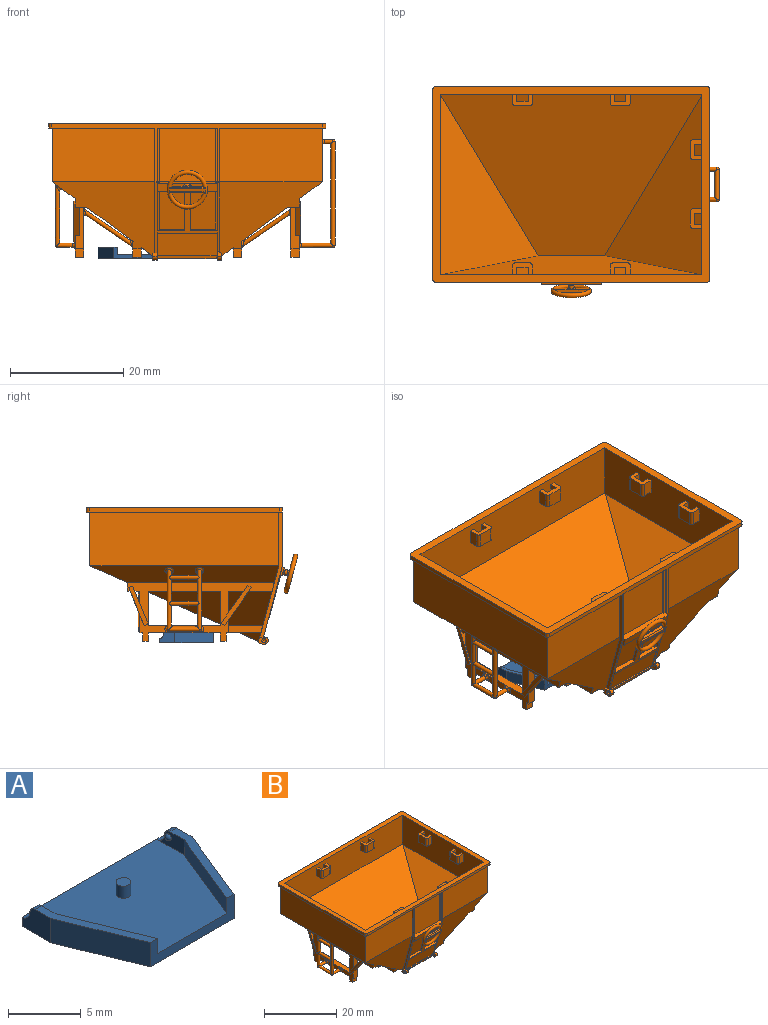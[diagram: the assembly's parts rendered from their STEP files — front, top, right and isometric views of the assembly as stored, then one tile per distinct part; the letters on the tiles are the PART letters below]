
ASSEMBLY  parts=2 mates=2
PART A: 22 faces, bbox 13.7x9.7x2 mm
  f0: plane 12.45x9.65mm, normal (0,0,1), area 99.5mm2, adj f3,f7,f8,f10,f11,f15,f20
  f1: plane 2.79x2.03mm, normal (-1,0,0), area 4.8mm2, adj f2,f6,f9,f15,f16,f19
  f2: plane 6.86x2.79mm, normal (-0.93,-0.38,0), area 15mm2, adj f1,f3,f6,f9
  f3: plane 8.13x2.03mm, normal (0,-1,0), area 7.9mm2, adj f0,f2,f4,f6,f8,f9,f10,f12
  f4: plane 6.86x2.79mm, normal (0.93,-0.38,0), area 15mm2, adj f3,f5,f6,f12
  f5: plane 2.79x2.03mm, normal (1,0,0), area 4.8mm2, adj f4,f6,f12,f15,f17,f18
  f6: plane 13.72x9.65mm, normal (0,0,-1), area 113.2mm2, adj f1,f2,f3,f4,f5,f15
  f7: plane 2.67x1.27mm, normal (1,0,0), area 2.3mm2, adj f0,f8,f9,f14,f16,f19
  f8: plane 6.98x2.84mm, normal (0.93,0.38,0), area 9.6mm2, adj f0,f3,f7,f9
  f9: plane 8.38x3.48mm, normal (0,0,1), area 5.7mm2, adj f1,f2,f3,f7,f8,f19
  f10: plane 6.98x2.84mm, normal (-0.93,0.38,0), area 9.6mm2, adj f0,f3,f11,f12
  f11: plane 2.67x1.27mm, normal (-1,0,0), area 2.3mm2, adj f0,f10,f12,f13,f17,f18
  f12: plane 8.38x3.48mm, normal (0,0,1), area 5.7mm2, adj f3,f4,f5,f10,f11,f18
  f13: sphere r=0.25mm, area 0.4mm2, adj f11
  f14: sphere r=0.25mm, area 0.4mm2, adj f7
  f15: plane 13.72x0.76mm, normal (0,1,0), area 10.5mm2, adj f0,f1,f5,f6,f16,f17
  f16: cylinder r=0.76mm len=0.76mm, axis (-1,0,0), area 0.8mm2, adj f1,f7,f15,f19
  f17: cylinder r=0.76mm len=0.76mm, axis (-1,0,0), area 0.8mm2, adj f5,f11,f15,f18
  f18: cylinder r=0.51mm len=0.64mm, axis (1,0,0), area 0.5mm2, adj f5,f11,f12,f17
  f19: cylinder r=0.51mm len=0.64mm, axis (1,0,0), area 0.5mm2, adj f1,f7,f9,f16
  f20: cylinder r=0.51mm len=1.02mm, axis (0,0,-1), area 3.2mm2, adj f0,f21
  f21: plane 1.02x1.02mm, normal (0,0,1), area 0.8mm2, adj f20
PART B: 349 faces, bbox 50.9x37.7x24.5 mm
  f0: plane 46.1x10.19mm, normal (0,1,0), area 461.8mm2, adj f1,f5,f7,f11,f13,f36,f37,f38
  f1: plane 2.54x1.52mm, normal (1,0,0), area 3.9mm2, adj f0,f2,f346,f348
  f2: cylinder r=0.51mm len=2.54mm, axis (0,0,-1), area 2mm2, adj f1,f3,f346,f348
  f3: plane 2.54x2.54mm, normal (0,1,0), area 6.5mm2, adj f2,f4,f346,f348
  f4: cylinder r=0.51mm len=2.54mm, axis (0,0,-1), area 2mm2, adj f3,f346,f347,f348
  f5: plane 2.54x1.27mm, normal (-1,0,0), area 3.2mm2, adj f0,f6,f346,f348
  f6: plane 2.54x2.03mm, normal (0,-1,0), area 5.2mm2, adj f5,f345,f346,f348
  f7: plane 2.54x1.52mm, normal (1,0,0), area 3.9mm2, adj f0,f8,f342,f344
  f8: cylinder r=0.51mm len=2.54mm, axis (0,0,-1), area 2mm2, adj f7,f9,f342,f344
  f9: plane 2.54x2.54mm, normal (0,1,0), area 6.5mm2, adj f8,f10,f342,f344
  f10: cylinder r=0.51mm len=2.54mm, axis (0,0,-1), area 2mm2, adj f9,f342,f343,f344
  f11: plane 2.54x1.27mm, normal (-1,0,0), area 3.2mm2, adj f0,f12,f342,f344
  f12: plane 2.54x2.03mm, normal (0,-1,0), area 5.2mm2, adj f11,f341,f342,f344
  f13: plane 31.57x17.18mm, normal (0.59,0,0.81), area 337.7mm2, adj f0,f14,f36,f340
  f14: plane 46.1x28.5mm, normal (0,-0.41,0.91), area 907.7mm2, adj f13,f15,f36,f37,f38,f340
  f15: plane 46.1x9.79mm, normal (0,-1,0), area 443.7mm2, adj f14,f16,f20,f22,f23,f24,f25,f26
  f16: plane 2.54x1.52mm, normal (1,0,0), area 3.9mm2, adj f15,f17,f22,f24
  f17: cylinder r=0.51mm len=2.54mm, axis (0,0,-1), area 2mm2, adj f16,f18,f22,f24
  f18: plane 2.54x2.54mm, normal (0,-1,0), area 6.5mm2, adj f17,f19,f22,f24
  f19: cylinder r=0.51mm len=2.54mm, axis (0,0,-1), area 2mm2, adj f18,f22,f24,f25
  f20: plane 2.54x1.27mm, normal (-1,0,0), area 3.2mm2, adj f15,f21,f22,f24
  f21: plane 2.54x2.03mm, normal (0,1,0), area 5.2mm2, adj f20,f22,f23,f24
  f22: plane 3.56x2.03mm, normal (0,0,-1), area 4.5mm2, adj f15,f16,f17,f18,f19,f20,f21,f23
  f23: plane 2.54x1.27mm, normal (1,0,0), area 3.2mm2, adj f15,f21,f22,f24
  f24: plane 3.56x2.03mm, normal (0,0,1), area 4.5mm2, adj f15,f16,f17,f18,f19,f20,f21,f23
  f25: plane 2.54x1.52mm, normal (-1,0,0), area 3.9mm2, adj f15,f19,f22,f24
  f26: plane 2.54x1.52mm, normal (1,0,0), area 3.9mm2, adj f15,f27,f32,f34
  f27: cylinder r=0.51mm len=2.54mm, axis (0,0,-1), area 2mm2, adj f26,f28,f32,f34
  f28: plane 2.54x2.54mm, normal (0,-1,0), area 6.5mm2, adj f27,f29,f32,f34
  f29: cylinder r=0.51mm len=2.54mm, axis (0,0,-1), area 2mm2, adj f28,f32,f34,f35
  f30: plane 2.54x1.27mm, normal (-1,0,0), area 3.2mm2, adj f15,f31,f32,f34
  f31: plane 2.54x2.03mm, normal (0,1,0), area 5.2mm2, adj f30,f32,f33,f34
  f32: plane 3.56x2.03mm, normal (0,0,-1), area 4.5mm2, adj f15,f26,f27,f28,f29,f30,f31,f33
  f33: plane 2.54x1.27mm, normal (1,0,0), area 3.2mm2, adj f15,f31,f32,f34
  f34: plane 3.56x2.03mm, normal (0,0,1), area 4.5mm2, adj f15,f26,f27,f28,f29,f30,f31,f33
  f35: plane 2.54x1.52mm, normal (-1,0,0), area 3.9mm2, adj f15,f29,f32,f34
  f36: plane 45.33x12.37mm, normal (0,0.97,0.26), area 365.5mm2, adj f0,f13,f14,f37
  f37: plane 31.57x17.18mm, normal (-0.59,0,0.81), area 337.7mm2, adj f0,f14,f36,f38
  f38: plane 31.81x9.9mm, normal (-1,0,0), area 307.3mm2, adj f0,f14,f15,f37,f39,f43,f45,f46
  f39: plane 2.54x1.52mm, normal (0,-1,0), area 3.9mm2, adj f38,f40,f45,f47
  f40: cylinder r=0.51mm len=2.54mm, axis (0,0,-1), area 2mm2, adj f39,f41,f45,f47
  f41: plane 2.54x2.54mm, normal (-1,0,0), area 6.5mm2, adj f40,f42,f45,f47
  f42: cylinder r=0.51mm len=2.54mm, axis (0,0,-1), area 2mm2, adj f41,f45,f47,f48
  f43: plane 2.54x1.27mm, normal (0,1,0), area 3.2mm2, adj f38,f44,f45,f47
  f44: plane 2.54x2.03mm, normal (1,0,0), area 5.2mm2, adj f43,f45,f46,f47
  f45: plane 3.56x2.03mm, normal (0,0,-1), area 4.5mm2, adj f38,f39,f40,f41,f42,f43,f44,f46
  f46: plane 2.54x1.27mm, normal (0,-1,0), area 3.2mm2, adj f38,f44,f45,f47
  f47: plane 3.56x2.03mm, normal (0,0,1), area 4.5mm2, adj f38,f39,f40,f41,f42,f43,f44,f46
  f48: plane 2.54x1.52mm, normal (0,1,0), area 3.9mm2, adj f38,f42,f45,f47
  f49: plane 2.54x1.52mm, normal (0,1,0), area 3.9mm2, adj f38,f50,f56,f58
  f50: cylinder r=0.51mm len=2.54mm, axis (0,0,-1), area 2mm2, adj f49,f51,f56,f58
  f51: plane 2.54x2.54mm, normal (-1,0,0), area 6.5mm2, adj f50,f52,f56,f58
  f52: cylinder r=0.51mm len=2.54mm, axis (0,0,-1), area 2mm2, adj f51,f56,f57,f58
  f53: plane 2.54x1.27mm, normal (0,-1,0), area 3.2mm2, adj f38,f54,f56,f58
  f54: plane 2.54x2.03mm, normal (1,0,0), area 5.2mm2, adj f53,f55,f56,f58
  f55: plane 2.54x1.27mm, normal (0,1,0), area 3.2mm2, adj f38,f54,f56,f58
  f56: plane 3.56x2.03mm, normal (0,0,-1), area 4.5mm2, adj f38,f49,f50,f51,f52,f53,f54,f55
  f57: plane 2.54x1.52mm, normal (0,-1,0), area 3.9mm2, adj f38,f52,f56,f58
  f58: plane 3.56x2.03mm, normal (0,0,1), area 4.5mm2, adj f38,f49,f50,f51,f52,f53,f54,f55
  f59: plane 48.9x34.61mm, normal (0,0,1), area 225.3mm2, adj f0,f15,f38,f60,f333,f334,f335,f336
  f60: cylinder r=0.51mm len=0.76mm, axis (0,0,-1), area 0.6mm2, adj f59,f61,f333,f339
  f61: plane 48.9x34.61mm, normal (0,0,-1), area 97mm2, adj f60,f62,f327,f328,f329,f330,f331,f332
  f62: plane 22.1x4mm, normal (-1,0,0), area 14.3mm2, adj f61,f63,f324,f325,f326,f327,f339
  f63: cylinder r=0.64mm len=0.38mm, axis (1,0,0), area 0.1mm2, adj f62,f64,f324,f339
  f64: plane 9.69x0.39mm, normal (1,0,0), area 3.7mm2, adj f63,f65,f321,f322,f323,f339
  f65: plane 10.67x0.64mm, normal (0,0,-1), area 6.6mm2, adj f64,f66,f317,f318,f319,f320,f321,f339
  f66: plane 9.69x0.39mm, normal (-1,0,0), area 3.7mm2, adj f65,f67,f68,f317,f323,f339
  f67: cylinder r=0.25mm len=0.38mm, axis (1,0,0), area 0mm2, adj f66,f317,f318,f323
  f68: cylinder r=0.64mm len=0.38mm, axis (1,0,0), area 0.1mm2, adj f66,f69,f332,f339
  f69: plane 12.09x3.24mm, normal (0,-0.97,-0.26), area 4.8mm2, adj f68,f70,f313,f314,f315,f316,f332
  f70: plane 0.52x0.25mm, normal (1,0,0), area 0.1mm2, adj f69,f71,f261,f312
  f71: plane 10.67x0.25mm, normal (0,0.26,-0.97), area 2.7mm2, adj f70,f72,f259,f260,f261,f316
  f72: plane 4.78x1.17mm, normal (1,0,0), area 1.5mm2, adj f71,f73,f255,f256,f257,f258,f260,f324
  f73: cylinder r=0.76mm len=0.96mm, axis (1,0,0), area 1.1mm2, adj f72,f74,f255,f258
  f74: plane 1.79x1.26mm, normal (-1,0,0), area 1.4mm2, adj f73,f75,f253,f255,f258,f325,f326
  f75: plane 1.02x0.53mm, normal (0,0.97,0.26), area 0.3mm2, adj f74,f76,f77,f252,f258
  f76: cylinder r=0.25mm len=0.8mm, axis (0,0.97,0.26), area 0.3mm2, adj f75,f77,f257,f258
  f77: plane 10.84x0.85mm, normal (0,0.26,-0.97), area 9.1mm2, adj f75,f76,f78,f251,f252,f257
  f78: cylinder r=0.25mm len=1.15mm, axis (0,-0.97,-0.26), area 0.4mm2, adj f77,f79,f247,f248,f249,f251
  f79: plane 0.76x0.15mm, normal (0,0.97,0.26), area 0mm2, adj f78,f80,f246,f247,f251
  f80: plane 1.97x1.26mm, normal (1,0,0), area 1.4mm2, adj f79,f81,f241,f242,f243,f244,f246,f247
  f81: plane 18.13x13.08mm, normal (0,-0.97,-0.26), area 127.6mm2, adj f80,f82,f177,f234,f235,f236,f237,f238
  f82: plane 33.34x4mm, normal (0.59,0,-0.81), area 147.4mm2, adj f81,f83,f177,f330
  f83: plane 47.63x6.58mm, normal (0,0.41,-0.91), area 314.5mm2, adj f82,f84,f176,f329
  f84: plane 33.34x4mm, normal (-0.59,0,-0.81), area 142.8mm2, adj f83,f85,f174,f175,f326,f328
  f85: plane 25.97x10.39mm, normal (-1,0,0), area 67.3mm2, adj f84,f86,f131,f132,f149,f150,f151,f152
  f86: plane 6.07x1.52mm, normal (0,1,0), area 9.2mm2, adj f85,f87,f173,f234
  f87: plane 15.75x8.86mm, normal (1,0,0), area 40.1mm2, adj f86,f88,f131,f149,f150,f151,f152,f155
  f88: bspline ~1.54x1.27mm, area 1.4mm2, adj f87,f89
  f89: cylinder r=0.38mm len=9.28mm, axis (-0.83,0,0.56), area 23.6mm2, adj f88,f90
  f90: bspline ~1.54x1.27mm, area 1.4mm2, adj f89,f91
  f91: plane 22.08x9.22mm, normal (-1,0,0), area 38.2mm2, adj f90,f92,f119,f120,f121,f122,f123,f124
  f92: plane 35.5x19.6mm, normal (0,0.41,-0.91), area 501.5mm2, adj f91,f93,f94,f95,f119,f120,f234,f235
  f93: plane 5.92x1.52mm, normal (0,-1,0), area 9mm2, adj f92,f236,f237,f239
  f94: plane 22.16x8.24mm, normal (-0.59,0,-0.81), area 149.1mm2, adj f92,f120,f234,f326
  f95: plane 21.45x8.86mm, normal (1,0,0), area 33.1mm2, adj f92,f96,f115,f116,f117,f118,f119,f120
  f96: plane 7.82x2.65mm, normal (-0.32,0,0.95), area 5.8mm2, adj f95,f97,f98,f117,f118,f130
  f97: plane 0.72x0.25mm, normal (-0.95,0,-0.32), area 0.2mm2, adj f96,f98,f115,f130
  f98: plane 18.02x6.75mm, normal (0,1,0), area 27.6mm2, adj f96,f97,f99,f100,f110,f111,f112,f113
  f99: plane 0.72x0.25mm, normal (-0.95,0,0.32), area 0.2mm2, adj f98,f116,f118,f130
  f100: plane 8.76x2.97mm, normal (-0.32,0,-0.95), area 6.7mm2, adj f98,f101,f110,f115,f117,f239
  f101: plane 7.34x1.52mm, normal (0,1,0), area 10mm2, adj f100,f102,f110,f111,f112,f113,f114,f234
  f102: plane 1.52x0.51mm, normal (0,0,-1), area 0.8mm2, adj f101,f103,f237,f239
  f103: plane 1.52x1.52mm, normal (0,1,0), area 2.3mm2, adj f102,f104,f237,f239
  f104: plane 1.52x1.02mm, normal (0,0,-1), area 1.5mm2, adj f103,f105,f237,f239
  f105: plane 1.52x1.52mm, normal (0,-1,0), area 2.3mm2, adj f104,f106,f237,f239
  f106: plane 12.7x1.52mm, normal (0,0,-1), area 19.4mm2, adj f105,f107,f237,f239
  f107: plane 1.52x1.52mm, normal (0,1,0), area 2.3mm2, adj f106,f108,f237,f239
  f108: plane 1.52x1.02mm, normal (0,0,-1), area 1.5mm2, adj f107,f109,f237,f239
  f109: plane 1.52x1.52mm, normal (0,-1,0), area 2.3mm2, adj f108,f237,f238,f239
  f110: plane 0.72x0.25mm, normal (0.95,0,-0.32), area 0.2mm2, adj f98,f100,f101,f111
  f111: plane 7.82x2.65mm, normal (0.32,0,0.95), area 5.8mm2, adj f98,f101,f110,f112,f117,f239
  f112: plane 7.82x2.65mm, normal (0.32,0,-0.95), area 5.8mm2, adj f98,f101,f111,f113,f117,f239
  f113: plane 0.72x0.25mm, normal (0.95,0,0.32), area 0.2mm2, adj f98,f101,f112,f114
  f114: plane 8.76x2.97mm, normal (-0.32,0,0.95), area 6.7mm2, adj f98,f101,f113,f116,f117,f239
  f115: plane 8.76x2.97mm, normal (0.32,0,-0.95), area 6.7mm2, adj f95,f97,f98,f100,f117,f130
  f116: plane 8.76x2.97mm, normal (0.32,0,0.95), area 6.7mm2, adj f95,f98,f99,f114,f117,f130
  f117: plane 16.26x6.32mm, normal (0,-1,0), area 25.2mm2, adj f95,f96,f100,f111,f112,f114,f115,f116
  f118: plane 7.82x2.65mm, normal (-0.32,0,-0.95), area 5.8mm2, adj f95,f96,f98,f99,f117,f130
  f119: plane 5.92x1.52mm, normal (0,-1,0), area 9mm2, adj f91,f92,f95,f120
  f120: plane 20.19x1.52mm, normal (0,0,1), area 21.1mm2, adj f91,f92,f94,f95,f119,f326
  f121: plane 6.14x1.52mm, normal (0,0,-1), area 9.4mm2, adj f91,f95,f122,f326
  f122: plane 1.52x1.52mm, normal (0,-1,0), area 2.3mm2, adj f91,f95,f121,f123
  f123: plane 1.52x1.02mm, normal (0,0,-1), area 1.5mm2, adj f91,f95,f122,f124
  f124: plane 1.52x1.52mm, normal (0,1,0), area 2.3mm2, adj f91,f95,f123,f125
  f125: plane 12.7x1.52mm, normal (0,0,-1), area 19.4mm2, adj f91,f95,f124,f126
  f126: plane 1.52x1.52mm, normal (0,-1,0), area 2.3mm2, adj f91,f95,f125,f127
  f127: plane 1.52x1.02mm, normal (0,0,-1), area 1.5mm2, adj f91,f95,f126,f128
  f128: plane 1.52x1.52mm, normal (0,1,0), area 2.3mm2, adj f91,f95,f127,f129
  f129: plane 1.52x0.51mm, normal (0,0,-1), area 0.8mm2, adj f91,f95,f128,f130
  f130: plane 7.34x1.52mm, normal (0,1,0), area 10mm2, adj f91,f95,f96,f97,f99,f115,f116,f118
  f131: plane 6.07x1.52mm, normal (0,-1,0), area 9.2mm2, adj f85,f87,f173,f234
  f132: torus R=0.76mm, axis (-1,0,0), area 0.6mm2, adj f85,f133,f147,f148
  f133: bspline ~0.95x0.42mm, area 0.3mm2, adj f132,f134,f147,f171
  f134: torus R=0.76mm, axis (-1,0,0), area 0.6mm2, adj f133,f135,f147,f148
  f135: plane 4.49x1.27mm, normal (-1,0,0), area 5.1mm2, adj f134,f136,f171,f173
  f136: torus R=0.76mm, axis (-1,0,0), area 0.6mm2, adj f135,f137,f138,f146
  f137: bspline ~0.95x0.42mm, area 0.3mm2, adj f136,f138,f171,f172
  f138: cylinder r=0.38mm len=2.75mm, axis (-1,0,0), area 6.1mm2, adj f136,f137,f139,f144,f145,f146,f172
  f139: cylinder r=0.38mm len=5.33mm, axis (0,1,0), area 11.9mm2, adj f138,f140,f141,f144,f145,f147
  f140: sphere r=0.38mm, area 0.1mm2, adj f139,f141,f147
  f141: cylinder r=0.38mm len=10.61mm, axis (0,0,1), area 22.5mm2, adj f139,f140,f142,f143,f147,f175
  f142: cylinder r=0.38mm len=5.33mm, axis (0,1,0), area 11.7mm2, adj f141,f145
  f143: cylinder r=0.38mm len=5.33mm, axis (0,-1,0), area 12.8mm2, adj f141,f145
  f144: sphere r=0.38mm, area 0.2mm2, adj f138,f139,f145
  f145: cylinder r=0.38mm len=10.61mm, axis (0,0,1), area 22.5mm2, adj f138,f139,f142,f143,f144,f174
  f146: bspline ~0.95x0.42mm, area 0.3mm2, adj f136,f138,f172,f173
  f147: cylinder r=0.38mm len=2.75mm, axis (1,0,0), area 6.1mm2, adj f132,f133,f134,f139,f140,f141,f148
  f148: bspline ~0.95x0.42mm, area 0.3mm2, adj f132,f134,f147,f173
  f149: plane 1.52x1.52mm, normal (0,-1,0), area 2.3mm2, adj f85,f87,f150,f171
  f150: plane 1.52x1.02mm, normal (0,0,-1), area 1.5mm2, adj f85,f87,f149,f151
  f151: plane 1.52x1.52mm, normal (0,1,0), area 2.3mm2, adj f85,f87,f150,f152
  f152: plane 1.52x0.51mm, normal (0,0,-1), area 0.8mm2, adj f85,f87,f151,f155
  f153: plane 0.71x0.29mm, normal (0,-0.37,-0.93), area 0.2mm2, adj f85,f154,f157,f159
  f154: plane 6.99x3.42mm, normal (-1,0,0), area 5.5mm2, adj f153,f157,f158,f159
  f155: plane 7.34x1.52mm, normal (0,1,0), area 9.6mm2, adj f85,f87,f152,f156,f157,f159,f234
  f156: plane 4.18x1.69mm, normal (1,0,0), area 2.6mm2, adj f155,f157,f159,f234
  f157: plane 6.7x2.71mm, normal (0,-0.93,0.37), area 3.6mm2, adj f85,f153,f154,f155,f156,f158,f234
  f158: plane 0.71x0.29mm, normal (0,0.37,0.93), area 0.2mm2, adj f85,f154,f157,f159
  f159: plane 6.7x2.71mm, normal (0,0.93,-0.37), area 5.3mm2, adj f85,f153,f154,f155,f156,f158,f234
  f160: plane 0.62x0.44mm, normal (0,-0.57,0.82), area 0.2mm2, adj f85,f161,f162,f165
  f161: plane 7.14x5.32mm, normal (-1,0,0), area 6.2mm2, adj f160,f162,f164,f165
  f162: plane 6.7x4.69mm, normal (0,0.82,0.57), area 5.5mm2, adj f85,f160,f161,f163,f164,f166,f234
  f163: plane 4.98x3.49mm, normal (1,0,0), area 4mm2, adj f162,f165,f166,f234
  f164: plane 0.62x0.44mm, normal (0,0.57,-0.82), area 0.2mm2, adj f85,f161,f162,f165
  f165: plane 6.7x4.69mm, normal (0,-0.82,-0.57), area 6.7mm2, adj f85,f160,f161,f163,f164,f166,f234
  f166: plane 7.34x1.52mm, normal (0,-1,0), area 10.2mm2, adj f85,f87,f162,f163,f165,f167,f234
  f167: plane 1.52x0.51mm, normal (0,0,-1), area 0.8mm2, adj f85,f87,f166,f168
  f168: plane 1.52x1.52mm, normal (0,-1,0), area 2.3mm2, adj f85,f87,f167,f169
  f169: plane 1.52x1.02mm, normal (0,0,-1), area 1.5mm2, adj f85,f87,f168,f170
  f170: plane 1.52x1.52mm, normal (0,1,0), area 2.3mm2, adj f85,f87,f169,f171
  f171: plane 12.72x1.54mm, normal (0,0,-1), area 19.4mm2, adj f85,f87,f133,f135,f137,f149,f170
  f172: torus R=0.76mm, axis (-1,0,0), area 0.6mm2, adj f85,f137,f138,f146
  f173: plane 12.72x1.54mm, normal (0,0,1), area 19.4mm2, adj f85,f86,f87,f131,f135,f146,f148
  f174: bspline ~1.52x1.52mm, area 2.3mm2, adj f84,f145
  f175: bspline ~1.52x1.52mm, area 2.3mm2, adj f84,f141
  f176: plane 39.62x1.52mm, normal (0,1,0), area 60.4mm2, adj f83,f85,f177,f234
  f177: plane 25.97x10.39mm, normal (1,0,0), area 67.3mm2, adj f81,f82,f176,f178,f183,f184,f185,f186
  f178: plane 1.52x1.52mm, normal (0,1,0), area 2.3mm2, adj f177,f179,f183,f233
  f179: plane 15.75x8.86mm, normal (-1,0,0), area 40.1mm2, adj f178,f180,f183,f184,f185,f188,f199,f200
  f180: bspline ~1.54x1.27mm, area 1.3mm2, adj f179,f181
  f181: cylinder r=0.38mm len=9.28mm, axis (-0.83,0,-0.56), area 23.6mm2, adj f180,f182
  f182: bspline ~1.54x1.27mm, area 1.4mm2, adj f181,f237
  f183: plane 1.52x1.02mm, normal (0,0,-1), area 1.5mm2, adj f177,f178,f179,f184
  f184: plane 1.52x1.52mm, normal (0,-1,0), area 2.3mm2, adj f177,f179,f183,f185
  f185: plane 1.52x0.51mm, normal (0,0,-1), area 0.8mm2, adj f177,f179,f184,f188
  f186: plane 0.62x0.44mm, normal (0,0.57,-0.82), area 0.2mm2, adj f177,f187,f190,f192
  f187: plane 7.14x5.32mm, normal (1,0,0), area 6.2mm2, adj f186,f190,f191,f192
  f188: plane 7.34x1.52mm, normal (0,-1,0), area 10.2mm2, adj f177,f179,f185,f189,f190,f192,f234
  f189: plane 4.98x3.49mm, normal (-1,0,0), area 4mm2, adj f188,f190,f192,f234
  f190: plane 6.7x4.69mm, normal (0,0.82,0.57), area 5.5mm2, adj f177,f186,f187,f188,f189,f191,f234
  f191: plane 0.62x0.44mm, normal (0,-0.57,0.82), area 0.2mm2, adj f177,f187,f190,f192
  f192: plane 6.7x4.69mm, normal (0,-0.82,-0.57), area 6.7mm2, adj f177,f186,f187,f188,f189,f191,f234
  f193: plane 0.71x0.29mm, normal (0,0.37,0.93), area 0.2mm2, adj f177,f194,f195,f198
  f194: plane 6.99x3.42mm, normal (1,0,0), area 5.5mm2, adj f193,f195,f197,f198
  f195: plane 6.7x2.71mm, normal (0,-0.93,0.37), area 3.6mm2, adj f177,f193,f194,f196,f197,f199,f234
  f196: plane 4.18x1.69mm, normal (-1,0,0), area 2.6mm2, adj f195,f198,f199,f234
  f197: plane 0.71x0.29mm, normal (0,-0.37,-0.93), area 0.2mm2, adj f177,f194,f195,f198
  f198: plane 6.7x2.71mm, normal (0,0.93,-0.37), area 5.3mm2, adj f177,f193,f194,f196,f197,f199,f234
  f199: plane 7.34x1.52mm, normal (0,1,0), area 9.6mm2, adj f177,f179,f195,f196,f198,f200,f234
  f200: plane 1.52x0.51mm, normal (0,0,-1), area 0.8mm2, adj f177,f179,f199,f201
  f201: plane 1.52x1.52mm, normal (0,1,0), area 2.3mm2, adj f177,f179,f200,f202
  f202: plane 1.52x1.02mm, normal (0,0,-1), area 1.5mm2, adj f177,f179,f201,f203
  f203: plane 1.52x1.52mm, normal (0,-1,0), area 2.3mm2, adj f177,f179,f202,f233
  f204: torus R=0.76mm, axis (1,0,0), area 0.6mm2, adj f177,f205,f227,f228
  f205: bspline ~0.95x0.42mm, area 0.3mm2, adj f204,f206,f227,f231
  f206: torus R=0.76mm, axis (1,0,0), area 0.6mm2, adj f205,f207,f227,f228
  f207: plane 4.49x1.27mm, normal (1,0,0), area 5.1mm2, adj f206,f208,f231,f233
  f208: torus R=0.76mm, axis (1,0,0), area 0.6mm2, adj f207,f209,f210,f226
  f209: bspline ~0.95x0.42mm, area 0.3mm2, adj f208,f210,f231,f232
  f210: cylinder r=0.38mm len=5.55mm, axis (1,0,0), area 12.8mm2, adj f208,f209,f211,f224,f225,f226,f232
  f211: cylinder r=0.38mm len=5.33mm, axis (0,-1,0), area 11.9mm2, adj f210,f212,f213,f224,f225,f227
  f212: sphere r=0.38mm, area 0.1mm2, adj f211,f213,f227
  f213: cylinder r=0.38mm len=18.29mm, axis (0,0,1), area 41.6mm2, adj f211,f212,f214,f215,f216,f217,f219,f223
  f214: cylinder r=0.38mm len=5.33mm, axis (0,-1,0), area 11.9mm2, adj f213,f224
  f215: cylinder r=0.38mm len=5.33mm, axis (0,-1,0), area 11.9mm2, adj f213,f224
  f216: sphere r=0.38mm, area 0.1mm2, adj f213,f217,f219
  f217: cylinder r=0.38mm len=1.52mm, axis (-1,0,0), area 3.2mm2, adj f213,f216,f218,f219
  f218: torus R=0.76mm, axis (-1,0,0), area 2mm2, adj f217,f330
  f219: cylinder r=0.38mm len=5.33mm, axis (0,-1,0), area 11.9mm2, adj f213,f216,f217,f220,f221,f224
  f220: sphere r=0.38mm, area 0.2mm2, adj f219,f221,f224
  f221: cylinder r=0.38mm len=1.52mm, axis (1,0,0), area 3.2mm2, adj f219,f220,f222,f224
  f222: torus R=0.76mm, axis (-1,0,0), area 2mm2, adj f221,f330
  f223: cylinder r=0.38mm len=5.33mm, axis (0,1,0), area 11.9mm2, adj f213,f224
  f224: cylinder r=0.38mm len=18.29mm, axis (0,0,1), area 41.6mm2, adj f210,f211,f214,f215,f219,f220,f221,f223
  f225: sphere r=0.38mm, area 0.3mm2, adj f210,f211,f224
  f226: bspline ~0.95x0.42mm, area 0.3mm2, adj f208,f210,f232,f233
  f227: cylinder r=0.38mm len=5.55mm, axis (1,0,0), area 12.8mm2, adj f204,f205,f206,f211,f212,f213,f228
  f228: bspline ~0.95x0.42mm, area 0.3mm2, adj f204,f206,f227,f233
  f229: plane 6.07x1.52mm, normal (0,-1,0), area 9.2mm2, adj f177,f179,f231,f234
  f230: plane 6.07x1.52mm, normal (0,1,0), area 9.2mm2, adj f177,f179,f231,f234
  f231: plane 12.72x1.54mm, normal (0,0,1), area 19.4mm2, adj f177,f179,f205,f207,f209,f229,f230
  f232: torus R=0.76mm, axis (1,0,0), area 0.6mm2, adj f177,f209,f210,f226
  f233: plane 12.72x1.54mm, normal (0,0,-1), area 19.4mm2, adj f177,f178,f179,f203,f207,f226,f228
  f234: plane 39.62x25.56mm, normal (0,0,-1), area 210.9mm2, adj f81,f85,f86,f87,f91,f92,f94,f95
  f235: plane 22.16x8.24mm, normal (0.59,0,-0.81), area 149.1mm2, adj f81,f92,f234,f236
  f236: plane 20.19x1.52mm, normal (0,0,1), area 21.1mm2, adj f81,f92,f93,f235,f237,f239
  f237: plane 21.72x8.86mm, normal (1,0,0), area 38.2mm2, adj f81,f92,f93,f101,f102,f103,f104,f105
  f238: plane 6.14x1.52mm, normal (0,0,-1), area 9.4mm2, adj f81,f109,f237,f239
  f239: plane 21.45x8.86mm, normal (-1,0,0), area 33.1mm2, adj f81,f92,f93,f100,f101,f102,f103,f104
  f240: cylinder r=0.25mm len=0.99mm, axis (0,1,0), area 0.3mm2, adj f81,f243,f315,f332
  f241: plane 4.45x2.24mm, normal (0.59,0,-0.81), area 6.5mm2, adj f80,f81,f92,f239,f246
  f242: cylinder r=0.51mm len=0.76mm, axis (-1,0,0), area 0.6mm2, adj f80,f243,f248,f316
  f243: plane 1.02x0.76mm, normal (0,0,1), area 0.1mm2, adj f80,f81,f240,f242,f315,f316
  f244: cylinder r=0.38mm len=0.76mm, axis (1,0,0), area 0.3mm2, adj f80,f245
  f245: sphere r=0.38mm, area 0.9mm2, adj f244
  f246: cylinder r=0.25mm len=0.49mm, axis (0.8,-0.16,0.59), area 0.1mm2, adj f79,f80,f92,f241,f251
  f247: plane 0.83x0.76mm, normal (0,0.26,-0.97), area 0.7mm2, adj f78,f79,f80,f248
  f248: cylinder r=0.76mm len=0.96mm, axis (-1,0,0), area 1.1mm2, adj f78,f80,f242,f247,f249,f316
  f249: cylinder r=0.25mm len=1.03mm, axis (0,-0.26,0.97), area 0.3mm2, adj f78,f248,f250,f257,f316
  f250: cylinder r=0.25mm len=0.56mm, axis (0,0.97,0.26), area 0.2mm2, adj f249,f256,f260,f316
  f251: cylinder r=0.25mm len=11.78mm, axis (-1,0,0), area 1.3mm2, adj f77,f78,f79,f92,f246,f252
  f252: plane 4.46x2.42mm, normal (-0.59,0,-0.81), area 6.7mm2, adj f75,f77,f92,f95,f251,f326
  f253: cylinder r=0.38mm len=0.76mm, axis (-1,0,0), area 0.3mm2, adj f74,f254
  f254: sphere r=0.38mm, area 0.9mm2, adj f253
  f255: cylinder r=0.51mm len=0.76mm, axis (1,0,0), area 0.6mm2, adj f72,f73,f74,f325
  f256: plane 10.41x0.25mm, normal (0,-0.26,0.97), area 2.6mm2, adj f72,f250,f257,f260
  f257: plane 10.41x0.74mm, normal (0,-0.97,-0.26), area 5.3mm2, adj f72,f76,f77,f249,f256
  f258: plane 0.83x0.76mm, normal (0,0.26,-0.97), area 0.7mm2, adj f72,f73,f74,f75,f76
  f259: plane 0.52x0.25mm, normal (-1,0,0), area 0.1mm2, adj f71,f261,f312,f324
  f260: plane 10.67x3.93mm, normal (0,-0.97,-0.26), area 43.3mm2, adj f71,f72,f250,f256,f316
  f261: plane 10.67x7.45mm, normal (0,-0.97,-0.26), area 12.7mm2, adj f70,f71,f259,f262,f264,f311,f312
  f262: plane 7.09x2.35mm, normal (-1,0,0), area 3.7mm2, adj f261,f263,f264,f312
  f263: plane 6.96x1.86mm, normal (0,0.97,0.26), area 7.3mm2, adj f262,f264,f311,f312
  f264: plane 10.67x0.98mm, normal (0,0.26,-0.97), area 10.1mm2, adj f261,f262,f263,f265,f266,f267,f305,f306
  f265: plane 7.05x2.23mm, normal (1,0,0), area 2.7mm2, adj f264,f310,f312,f324
  f266: plane 1.57x0.76mm, normal (-1,0,0), area 0.6mm2, adj f264,f267,f323,f324
  f267: plane 5.33x1.47mm, normal (0,-0.97,-0.26), area 7.2mm2, adj f264,f266,f268,f323
  f268: torus R=0.76mm, axis (0,-0.97,-0.26), area 1.5mm2, adj f267,f269,f305
  f269: cylinder r=0.51mm len=1.18mm, axis (0,0.97,0.26), area 1.8mm2, adj f268,f270,f300,f301,f302,f303,f304
  f270: bspline ~0.59x0.26mm, area 0.1mm2, adj f269,f271,f300
  f271: plane 6.3x0.52mm, normal (0,0.26,-0.97), area 2.9mm2, adj f270,f272,f292,f297,f298,f299,f304
  f272: plane 2.61x0.98mm, normal (0,0.97,0.26), area 2.5mm2, adj f271,f273,f274,f275,f276,f277,f300
  f273: plane 0.04x0mm, normal (0,0.26,-0.97), area 0mm2, adj f272,f274,f299
  f274: plane 0.51x0.15mm, normal (1,0,0), area 0mm2, adj f272,f273,f299
  f275: plane 0.51x0.15mm, normal (1,0,0), area 0mm2, adj f272,f276,f299
  f276: plane 0.04x0mm, normal (0,-0.26,0.97), area 0mm2, adj f272,f275,f299
  f277: plane 6.3x0.52mm, normal (0,-0.26,0.97), area 2.9mm2, adj f272,f278,f292,f297,f299,f301,f302
  f278: cylinder r=0.25mm len=5.54mm, axis (1,0,0), area 2.2mm2, adj f277,f279,f290,f291
  f279: plane 6.62x1.25mm, normal (0,-0.97,-0.26), area 3.4mm2, adj f278,f280,f281,f282,f283,f284,f285,f286
  f280: plane 0.52x0.16mm, normal (-1,0,0), area 0mm2, adj f279,f281,f297
  f281: bspline ~0.17x0.09mm, area 0mm2, adj f279,f280,f297
  f282: bspline ~0.17x0.09mm, area 0mm2, adj f279,f283,f299
  f283: plane 0.52x0.16mm, normal (1,0,0), area 0mm2, adj f279,f282,f299
  f284: plane 0.52x0.16mm, normal (1,0,0), area 0mm2, adj f279,f285,f299
  f285: bspline ~0.17x0.08mm, area 0mm2, adj f279,f284,f299
  f286: bspline ~0.39x0.32mm, area 0mm2, adj f279,f298,f299
  f287: bspline ~0.4x0.32mm, area 0mm2, adj f279,f297,f298
  f288: bspline ~0.17x0.08mm, area 0mm2, adj f279,f289,f297
  f289: plane 0.52x0.16mm, normal (-1,0,0), area 0mm2, adj f279,f288,f297
  f290: bspline ~0.36x0.31mm, area 0mm2, adj f278,f279,f297
  f291: bspline ~0.39x0.31mm, area 0mm2, adj f278,f279,f299
  f292: plane 2.61x0.98mm, normal (0,0.97,0.26), area 2.5mm2, adj f271,f277,f293,f294,f295,f296,f303
  f293: plane 0.04x0mm, normal (0,-0.26,0.97), area 0mm2, adj f292,f294,f297
  f294: plane 0.51x0.15mm, normal (-1,0,0), area 0mm2, adj f292,f293,f297
  f295: plane 0.51x0.15mm, normal (-1,0,0), area 0mm2, adj f292,f296,f297
  f296: plane 0.04x0mm, normal (0,0.26,-0.97), area 0mm2, adj f292,f295,f297
  f297: torus R=3.17mm, axis (0,-0.97,-0.26), area 46.5mm2, adj f271,f277,f280,f281,f287,f288,f289,f290
  f298: cylinder r=0.25mm len=5.54mm, axis (-1,0,0), area 2.2mm2, adj f271,f279,f286,f287
  f299: torus R=3.17mm, axis (0,-0.97,-0.26), area 1.3mm2, adj f271,f273,f274,f275,f276,f277,f282,f283
  f300: torus R=0.76mm, axis (0,-0.97,-0.26), area 0.3mm2, adj f269,f270,f272,f301
  f301: bspline ~0.59x0.29mm, area 0.1mm2, adj f269,f277,f300
  f302: bspline ~0.59x0.29mm, area 0.1mm2, adj f269,f277,f303
  f303: torus R=0.76mm, axis (0,-0.97,-0.26), area 0.3mm2, adj f269,f292,f302,f304
  f304: bspline ~0.59x0.26mm, area 0.1mm2, adj f269,f271,f303
  f305: plane 5.33x1.47mm, normal (0,-0.97,-0.26), area 7.2mm2, adj f264,f268,f314,f323
  f306: plane 6.96x1.86mm, normal (0,-0.97,-0.26), area 2.7mm2, adj f264,f307,f312,f313
  f307: plane 7.02x2.11mm, normal (-1,0,0), area 1.8mm2, adj f264,f306,f308,f312
  f308: plane 9.91x6.96mm, normal (0,-0.97,-0.26), area 71.3mm2, adj f264,f307,f309,f312
  f309: plane 7.02x2.11mm, normal (1,0,0), area 1.8mm2, adj f264,f308,f310,f312
  f310: plane 6.96x1.86mm, normal (0,-0.97,-0.26), area 2.7mm2, adj f264,f265,f309,f312
  f311: plane 7.09x2.35mm, normal (1,0,0), area 3.7mm2, adj f261,f263,f264,f312
  f312: plane 10.67x0.74mm, normal (0,-0.26,0.97), area 7.4mm2, adj f70,f259,f261,f262,f263,f265,f306,f307
  f313: plane 7.05x2.23mm, normal (-1,0,0), area 2.7mm2, adj f69,f264,f306,f312
  f314: plane 1.57x0.76mm, normal (1,0,0), area 0.6mm2, adj f69,f264,f305,f323
  f315: cylinder r=0.25mm len=0.64mm, axis (1,0,0), area 0.2mm2, adj f69,f240,f243,f316,f332
  f316: plane 4.78x1.11mm, normal (-1,0,0), area 1.2mm2, adj f69,f71,f242,f243,f248,f249,f250,f260
  f317: plane 9.53x0.38mm, normal (0,-1,0), area 3.6mm2, adj f65,f66,f67,f318
  f318: plane 9.59x0.25mm, normal (-1,0,0), area 2.4mm2, adj f65,f67,f317,f319,f323
  f319: plane 9.91x9.53mm, normal (0,-1,0), area 94.4mm2, adj f65,f318,f320,f323
  f320: plane 9.59x0.25mm, normal (1,0,0), area 2.4mm2, adj f65,f319,f321,f322,f323
  f321: plane 9.53x0.38mm, normal (0,-1,0), area 3.6mm2, adj f64,f65,f320,f322
  f322: cylinder r=0.25mm len=0.38mm, axis (1,0,0), area 0mm2, adj f64,f320,f321,f323
  f323: plane 10.67x0.98mm, normal (0,-0.26,0.97), area 10.6mm2, adj f64,f66,f67,f266,f267,f305,f314,f318
  f324: plane 12.41x3.33mm, normal (0,-0.97,-0.26), area 4.9mm2, adj f62,f63,f72,f259,f265,f266,f325
  f325: plane 1.02x0.76mm, normal (0,0,1), area 0.5mm2, adj f62,f72,f74,f255,f324,f326
  f326: plane 18.1x13.05mm, normal (0,-0.97,-0.26), area 127.6mm2, adj f62,f74,f84,f85,f91,f94,f95,f120
  f327: plane 18.1x9.53mm, normal (0,-1,0), area 172.4mm2, adj f61,f62,f326,f328
  f328: plane 33.34x9.53mm, normal (-1,0,0), area 317.5mm2, adj f61,f84,f327,f329
  f329: plane 47.63x9.53mm, normal (0,1,0), area 453.6mm2, adj f61,f83,f328,f330
  f330: plane 33.34x9.53mm, normal (1,0,0), area 313.9mm2, adj f61,f82,f218,f222,f329,f331
  f331: plane 18.1x9.53mm, normal (0,-1,0), area 172.4mm2, adj f61,f81,f330,f332
  f332: plane 21.84x3.94mm, normal (1,0,0), area 14.1mm2, adj f61,f68,f69,f81,f240,f315,f331,f339
  f333: plane 33.59x0.76mm, normal (-1,0,0), area 25.6mm2, adj f59,f60,f61,f334
  f334: cylinder r=0.51mm len=0.76mm, axis (0,0,-1), area 0.6mm2, adj f59,f61,f333,f335
  f335: plane 47.88x0.76mm, normal (0,1,0), area 36.5mm2, adj f59,f61,f334,f336
  f336: cylinder r=0.51mm len=0.76mm, axis (0,0,1), area 0.6mm2, adj f59,f61,f335,f337
  f337: plane 33.59x0.76mm, normal (1,0,0), area 25.6mm2, adj f59,f61,f336,f338
  f338: cylinder r=0.51mm len=0.76mm, axis (0,0,1), area 0.6mm2, adj f59,f61,f337,f339
  f339: plane 47.88x10.29mm, normal (0,-1,0), area 43.7mm2, adj f59,f60,f61,f62,f63,f64,f65,f66
  f340: plane 31.81x9.9mm, normal (1,0,0), area 315mm2, adj f0,f13,f14,f15,f59
  f341: plane 2.54x1.27mm, normal (1,0,0), area 3.2mm2, adj f0,f12,f342,f344
  f342: plane 3.56x2.03mm, normal (0,0,-1), area 4.5mm2, adj f0,f7,f8,f9,f10,f11,f12,f341
  f343: plane 2.54x1.52mm, normal (-1,0,0), area 3.9mm2, adj f0,f10,f342,f344
  f344: plane 3.56x2.03mm, normal (0,0,1), area 4.5mm2, adj f0,f7,f8,f9,f10,f11,f12,f341
  f345: plane 2.54x1.27mm, normal (1,0,0), area 3.2mm2, adj f0,f6,f346,f348
  f346: plane 3.56x2.03mm, normal (0,0,-1), area 4.5mm2, adj f0,f1,f2,f3,f4,f5,f6,f345
  f347: plane 2.54x1.52mm, normal (-1,0,0), area 3.9mm2, adj f0,f4,f346,f348
  f348: plane 3.56x2.03mm, normal (0,0,1), area 4.5mm2, adj f0,f1,f2,f3,f4,f5,f6,f345
PLACE A t=(-17.87,6.13,-3.29)mm
PLACE B t=(-8.98,2.42,-3.04)mm fixed
MATE planar A.f20 <-> B.f125  axis (0,0,1) through (-17.87,3.91,-1.51)mm
MATE parallel A.f15 <-> B.f126  axis (0,1,0) through (-17.87,6.9,-2.91)mm
